# Revit family: PipeAccessories_Valve-Balancing_TA-Hydronics_STAF_DN65-150
name_source: partatom
category: Pipe Accessories
units: mm (PartAtom-declared; Revit-internal decimal feet)

## family parameters
Always vertical = Yes
Cut with Voids When Loaded = No
OmniClass Number = 23.65.55.14.17
OmniClass Title = Adjusting/Controlling Valves for Liquid Services
Part Type = Valve - Breaks Into
Round Connector Dimension = Use Diameter
Shared = No
Work Plane-Based = No

## types (1)
- TA-Hydronics_STAF_DN65-150
    Angle = 68.00°
    BodyMaterial = TA-Hydronics_DuctileIron
    BonnetMaterial = TA-Hydronics_CastIron
    ConnectorDescription = DN 65-150: Flanges according to EN-1092-2, type 21.
    Description = Manual balancing valve
    HandleMaterial = TA-Hydronics_Polyamide
    LeverHeight = 30 mm  [stored 0.0984252 ft]
    LeverPosition = 26 mm
    Lookup Table Name = PipeAccessories_Valve-Balancing_TA-Hydronics_STAF_DN65-150
    Manufacturer = Tour&Andersson
    MaximumWorkingTemperature = 120°C
    MinimumWorkingTemperature = -10°C
    Model = STAF-CastIron
    ModifiedIssue_ANZRS = 20141016.54 $
    SpindleAlignment = 30 mm  [stored 0.0984252 ft]
    SpindleDiameter = 70 mm  [stored 0.229659 ft]
    SpindlePosition = 20 mm  [stored 0.0656168 ft]
    SpindleStackDiameter_A = 21 mm  [stored 0.0688976 ft]
    SpindleStackDiameter_B = 50 mm
    Type Comments = Flanged ends
    URL = http://www.tahydronics.com

note: [stored X ft] marks values corroborated as IEEE doubles in the binary element streams (Revit-internal decimal feet)

## geometry (parser evidence)
native form markers: Sweep x2
no freeform markers — native parametric forms only
